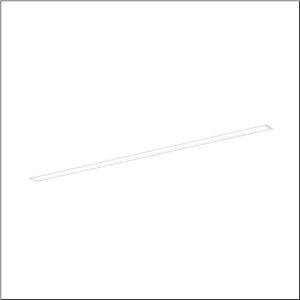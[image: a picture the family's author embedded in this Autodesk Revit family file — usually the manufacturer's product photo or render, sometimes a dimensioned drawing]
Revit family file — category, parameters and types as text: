
# Revit family: silica_r__21_51mx13db35wb_9931
name_source: partatom
category: Lighting Fixtures
units: mm (PartAtom-declared; Revit-internal decimal feet)

## family parameters
Cut with Voids When Loaded = No
Host = Face
Light Source = No
Part Type = Normal
Room Calculation Point = No
Round Connector Dimension = Use Diameter
Shared = No

## types (1)
- --- (1 x LED, 4100 lm, 30.1 W, 3000K)
    Apparent Load = 30 VA
    CIE Flux Codes = 78 96 99 100 100
    Color Rendering = 80
    Color Temperature = 3000K
    Default Elevation = 1800 mm
    Description = Silica® 21, office luminaire, primary optical cover: prismatic diffuser, of PMMA, CAT 2 (L<= 3000cd/m²), light emission: direct distribution, primary light characteristic: symmetric, installation type: recessed, LED, rated luminous flux: 4.100lm, luminous efficacy: 136lm/W, light colour: 830, colour temperature: 3000K, with terminal, 3+2-pole, max. 2.5mm², mains connection: 220..240V, AC, 50/60Hz, rated input power: 30.1W, luminaire housing, of aluminium, traffic white (RAL 9016), length: 1.528mm, width: 79mm, height: 53mm, protection rating (complete): IP20, insulation class (complete): insulation class I (protective earthing), certification: CE, permissible operating ambient temperature: 0..+35°C, standard: EN 50419, packaging unit: 1 piece
    Height = 0 mm  [stored 0 ft]
    Lamp = 1 x LED
    Lamp Light Flux = 4100 lm
    Lamp Power = 30.1 W
    Lamp count = 1
    Length = 1527 mm
    Luminous efficacy = 136 lm/W
    Manufacturer = Siteco
    ModVariant = No
    Model = 51MX13DB35WB
    Mounting Place = Ceiling
    Mounting Type = Recessed
    Number of Poles = 1
    OnlyDefault = Yes
    Power Factor = 1
    Product Name = Silica® 21
    Product group = office luminaire | ceiling recessed
    ProductGroupID = 401
    Protection Class = Protection class I
    Protection Degree = IP 20
    RLX_Detail_Level = 1
    RLX_Emergency_Light_Flux = 0 lm
    RLX_Emergency_Type = 0
    RLX_Emergency_Type_DB = No
    RlxData = <blob elided: 14217 chars, md5=de508b01>
    Socket = socket
    Standby Power = 0 W
    System Light Flux = 4100 lm
    System Power = 30 W
    Type Comments = factory setting: luminous flux: 100 % | dim-lin: 254 | 345 mA
    Type Image = l_1251692.jpg
    URL = http://relux.com
    VarID = @adj_049403
    Voltage = 0 V
    Weight = 0.00 kg
    Width = 79 mm

note: [stored X ft] marks values corroborated as IEEE doubles in the binary element streams (Revit-internal decimal feet)

## geometry (parser evidence)
native form markers: Sweep x13
no freeform markers — native parametric forms only
